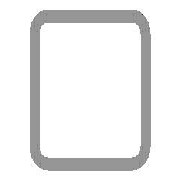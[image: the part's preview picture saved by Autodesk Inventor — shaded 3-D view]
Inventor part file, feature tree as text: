
AUTODESK INVENTOR PART (.ipt)
format: ipt  version: 2025 (Build 290162010, 162A)  size: 132,608 bytes
history: native  units: mm (DEFAULTED — no unit token found)
features: other x4, sketch x1, plane x1
ambient origin geometry x8: Origin, YZ Plane, XZ Plane, XY Plane, X Axis, Y Axis, Z Axis, Center Point
bodies: Solid1 (feature_tree), Body (feature_tree)
feature tree (6):
  parser-record x1  (decoder bookkeeping rows leaked as tree rows — omitted from the tree; the rows remain in map.json)
  other  "Driven Length"
  other  "Start Plane"
  other  "End Plane"
  sketch  "Sketch3"  dims[d3=1500.0mm d4=0.0mm d7=4.0mm d9=40.0mm d11=40.0mm d12=2.0mm d13=-0.0mm d14=1500.0mm d15=20.0mm d16=20.0mm d17=90.0deg d18=1500.0mm]
  plane  "Work Plane3"
